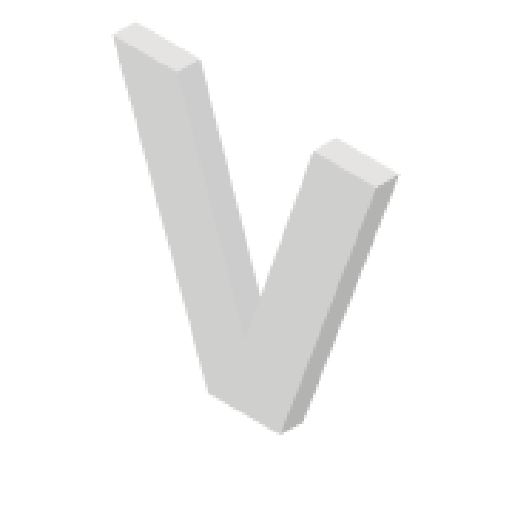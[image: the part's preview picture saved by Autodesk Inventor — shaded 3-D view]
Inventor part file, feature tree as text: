
AUTODESK INVENTOR PART (.ipt)
format: ipt  version: 2025 (Build 290162000, 162)  size: 114,688 bytes
history: native  units: mm
features: reference x7, extrude x2, sketch x2, other x2, projected_geometry x1
ambient origin geometry x8: Origin, YZ Plane, XZ Plane, XY Plane, X Axis, Y Axis, Z Axis, Center Point
bodies: Solid1 (feature_tree)
feature tree (14):
  extrude  "Extrusion1"  Depth=0.6mm TaperAngle=0.0deg
  extrude  "Extrusion2"  Depth=10.0mm TaperAngle=0.0deg
  sketch  "Sketch1"  dims[d0=40.0mm d1=0.6mm d2=0.0mm]
  sketch  "Sketch2"  dims[d3=0.1mm d4=10.0mm d5=0.0mm]
  projected_geometry  "Projected Loop1"
  reference  "Reference1"
  reference  "Reference2"
  reference  "Reference3"
  reference  "Reference4"
  reference  "Reference5"
  reference  "Reference6"
  reference  "Reference7"
  other  "USB_C_PD_PPS_sink_with_enclosure.iam"
  other  "display_cover_2:1"
